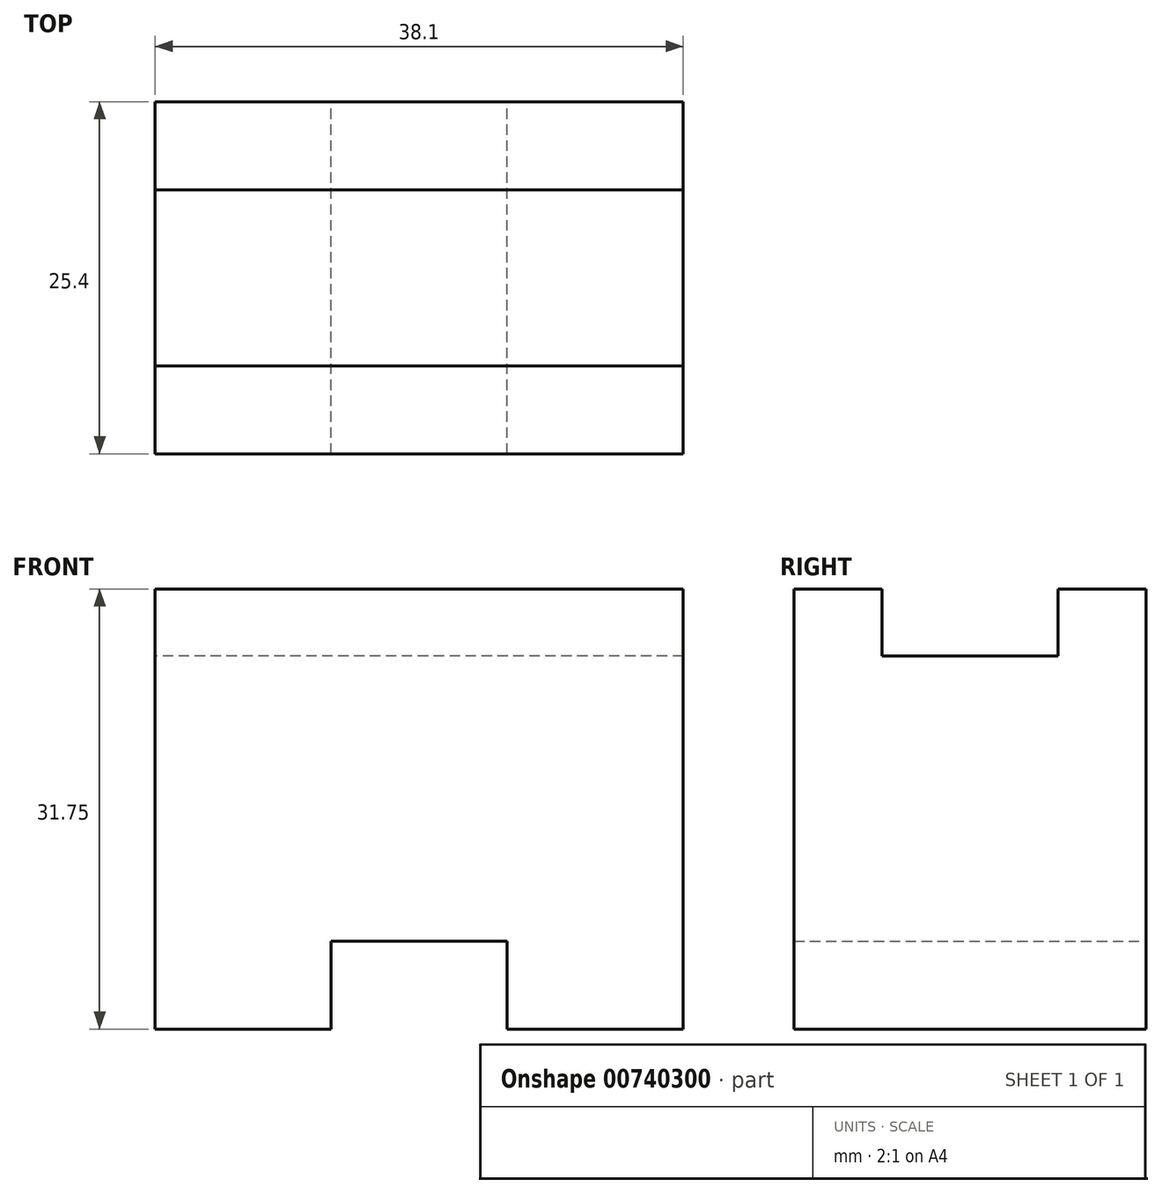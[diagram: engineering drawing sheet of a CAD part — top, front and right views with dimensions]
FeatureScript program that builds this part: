
annotation { "Feature Type Name" : "Feature", "Feature Type Description" : "" }
export const myFeature = defineFeature(function(context is Context, id is Id, definition is map)
    precondition{}
    {
        {
            var Q0;
            Q0=qCreatedBy(makeId("Front.planeOp"),FACE);
            var sketch = newSketch(context, id + "F0", { "sketchPlane" : qUnion([Q0])});
            skLineSegment(sketch, "E0", {"start": v(0, 0) * mm, "end": v(0, 31.75) * mm});
            skLineSegment(sketch, "E1", {"start": v(0, 31.75) * mm, "end": v(38.1, 31.75) * mm});
            skLineSegment(sketch, "E2", {"start": v(38.1, 31.75) * mm, "end": v(38.1, 0) * mm});
            skLineSegment(sketch, "E3", {"start": v(38.1, 0) * mm, "end": v(0, 0) * mm});
            skSolve(sketch);
        }
        {
            var Q0;
            Q0 = qSketchRegion(id + "F0", true);
            extrude(context, id + "F1", {"entities" : qUnion([Q0]), "depth" : 25.4 * mm, "offsetDistance" : 25.4 * mm});
        }
        {
            var Q0;
            Q0=qCreatedBy(makeId("Front.planeOp"),FACE);
            var sketch = newSketch(context, id + "F2", { "sketchPlane" : qUnion([Q0])});
            skLineSegment(sketch, "E4", {"start": v(12.7, 0) * mm, "end": v(12.7, 6.35) * mm});
            skLineSegment(sketch, "E5", {"start": v(12.7, 6.35) * mm, "end": v(25.4, 6.35) * mm});
            skLineSegment(sketch, "E6", {"start": v(25.4, 6.35) * mm, "end": v(25.4, 0) * mm});
            skLineSegment(sketch, "E7", {"start": v(25.4, 0) * mm, "end": v(12.7, 0) * mm});
            skSolve(sketch);
        }
        {
            var Q0;
            Q0 = qSketchRegion(id + "F2", true);
            extrude(context, id + "F3", {"entities" : qUnion([Q0]), "operationType" : NewBodyOperationType.REMOVE, "depth" : 25.4 * mm, "offsetDistance" : 25.4 * mm});
        }
        {
            var Q0;
            Q0=qCreatedBy(makeId("Right.planeOp"),FACE);
            var sketch = newSketch(context, id + "F4", { "sketchPlane" : qUnion([Q0])});
            skLineSegment(sketch, "E8", {"start": v(-6.35, 33.25) * mm, "end": v(-6.35, 26.9) * mm});
            skLineSegment(sketch, "E9", {"start": v(-6.35, 26.9) * mm, "end": v(-19.05, 26.9) * mm});
            skLineSegment(sketch, "E10", {"start": v(-19.05, 26.9) * mm, "end": v(-19.05, 33.25) * mm});
            skLineSegment(sketch, "E11", {"start": v(-19.05, 33.25) * mm, "end": v(-6.35, 33.25) * mm});
            skSolve(sketch);
        }
        {
            var Q0;
            Q0 = qSketchRegion(id + "F4", true);
            extrude(context, id + "F5", {"entities" : qUnion([Q0]), "operationType" : NewBodyOperationType.REMOVE, "depth" : 38.1 * mm, "offsetDistance" : 25.4 * mm});
        }
    });
